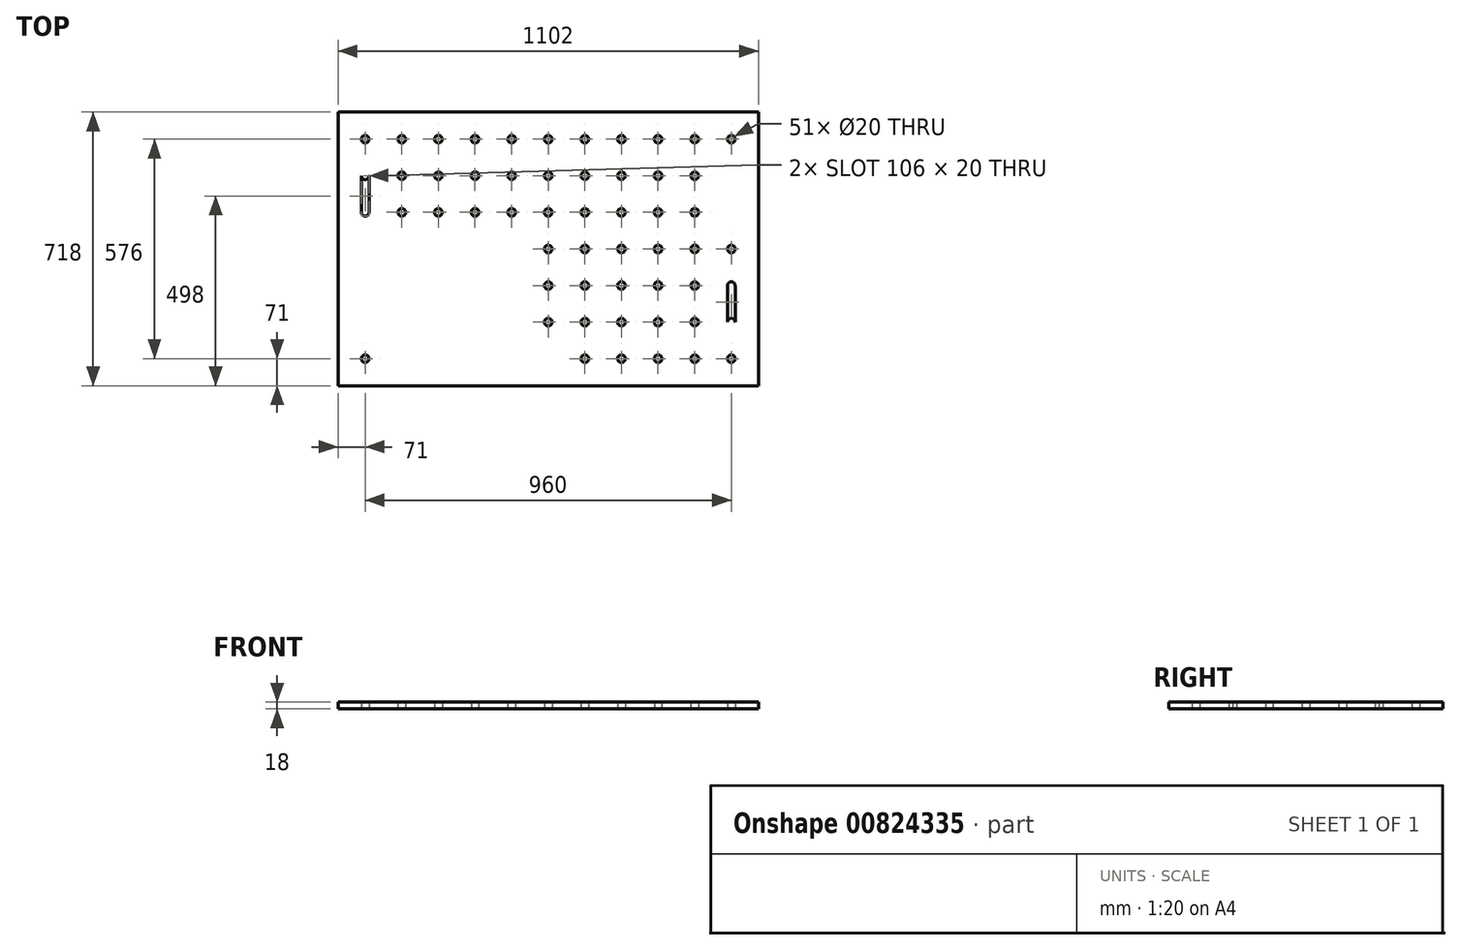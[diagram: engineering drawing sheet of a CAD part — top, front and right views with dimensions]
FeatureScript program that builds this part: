
annotation { "Feature Type Name" : "Feature", "Feature Type Description" : "" }
export const myFeature = defineFeature(function(context is Context, id is Id, definition is map)
    precondition{}
    {
        {
            var Q0;
            Q0=qCreatedBy(makeId("Top.planeOp"),FACE);
            var sketch = newSketch(context, id + "F0", { "sketchPlane" : qUnion([Q0])});
            skLineSegment(sketch, "E0.bottom", {"start": v(-551, -359) * mm, "end": v(551, -359) * mm});
            skLineSegment(sketch, "E0.top", {"start": v(-551, 359) * mm, "end": v(551, 359) * mm});
            skLineSegment(sketch, "E0.left", {"start": v(-551, -359) * mm, "end": v(-551, 359) * mm});
            skLineSegment(sketch, "E0.right", {"start": v(551, -359) * mm, "end": v(551, 359) * mm});
            skPoint(sketch, "E0.middle", {"position": v(0, 0) * mm});
            skSolve(sketch);
        }
        {
            var Q0;
            Q0=makeQuery(id+"F0.imprint","IMPRINT",FACE,{"disambiguationData":[TD([[makeQuery(id+"F0.imprint","IMPRINT",EDGE,{"derivedFrom":sQuery(id+"F0.wireOp",EDGE,"E0.bottom")}),1.0]])]});
            var sketch = newSketch(context, id + "F1", { "sketchPlane" : qUnion([Q0])});
            skLineSegment(sketch, "E1", {"start": v(0, 268.38) * mm, "end": v(0, -265.3) * mm, "construction": true});
            skLineSegment(sketch, "E2", {"start": v(473.2, 0) * mm, "end": v(-470.36, 0) * mm, "construction": true});
            skCircle(sketch, "E3", {"center": v(0, 0) * mm, "radius": 10 * mm});
            skCircle(sketch, "E4", {"center": v(96, 0) * mm, "radius": 10 * mm});
            skCircle(sketch, "E5.0.1.0", {"center": v(0, 96) * mm, "radius": 10 * mm});
            skCircle(sketch, "E5.0.1.1", {"center": v(96, 96) * mm, "radius": 10 * mm});
            skCircle(sketch, "E5.0.2.0", {"center": v(0, 192) * mm, "radius": 10 * mm});
            skCircle(sketch, "E5.0.2.1", {"center": v(96, 192) * mm, "radius": 10 * mm});
            skCircle(sketch, "E5.0.3.0", {"center": v(0, 288) * mm, "radius": 10 * mm});
            skCircle(sketch, "E5.0.3.1", {"center": v(96, 288) * mm, "radius": 10 * mm});
            skCircle(sketch, "E5.1.0.1", {"center": v(192, 0) * mm, "radius": 10 * mm});
            skCircle(sketch, "E5.1.1.0", {"center": v(96, 96) * mm, "radius": 10 * mm});
            skCircle(sketch, "E5.1.1.1", {"center": v(192, 96) * mm, "radius": 10 * mm});
            skCircle(sketch, "E5.1.2.0", {"center": v(96, 192) * mm, "radius": 10 * mm});
            skCircle(sketch, "E5.1.2.1", {"center": v(192, 192) * mm, "radius": 10 * mm});
            skCircle(sketch, "E5.1.3.0", {"center": v(96, 288) * mm, "radius": 10 * mm});
            skCircle(sketch, "E5.1.3.1", {"center": v(192, 288) * mm, "radius": 10 * mm});
            skCircle(sketch, "E5.2.0.0", {"center": v(192, 0) * mm, "radius": 10 * mm});
            skCircle(sketch, "E5.2.0.1", {"center": v(288, 0) * mm, "radius": 10 * mm});
            skCircle(sketch, "E5.2.1.0", {"center": v(192, 96) * mm, "radius": 10 * mm});
            skCircle(sketch, "E5.2.1.1", {"center": v(288, 96) * mm, "radius": 10 * mm});
            skCircle(sketch, "E5.2.2.0", {"center": v(192, 192) * mm, "radius": 10 * mm});
            skCircle(sketch, "E5.2.2.1", {"center": v(288, 192) * mm, "radius": 10 * mm});
            skCircle(sketch, "E5.2.3.0", {"center": v(192, 288) * mm, "radius": 10 * mm});
            skCircle(sketch, "E5.2.3.1", {"center": v(288, 288) * mm, "radius": 10 * mm});
            skCircle(sketch, "E5.3.0.0", {"center": v(288, 0) * mm, "radius": 10 * mm});
            skCircle(sketch, "E5.3.0.1", {"center": v(384, 0) * mm, "radius": 10 * mm});
            skCircle(sketch, "E5.3.1.0", {"center": v(288, 96) * mm, "radius": 10 * mm});
            skCircle(sketch, "E5.3.1.1", {"center": v(384, 96) * mm, "radius": 10 * mm});
            skCircle(sketch, "E5.3.2.0", {"center": v(288, 192) * mm, "radius": 10 * mm});
            skCircle(sketch, "E5.3.2.1", {"center": v(384, 192) * mm, "radius": 10 * mm});
            skCircle(sketch, "E5.3.3.0", {"center": v(288, 288) * mm, "radius": 10 * mm});
            skCircle(sketch, "E5.3.3.1", {"center": v(384, 288) * mm, "radius": 10 * mm});
            skCircle(sketch, "E5.4.0.0", {"center": v(384, 0) * mm, "radius": 10 * mm});
            skCircle(sketch, "E5.4.0.1", {"center": v(480, 0) * mm, "radius": 10 * mm});
            skCircle(sketch, "E5.4.1.0", {"center": v(384, 96) * mm, "radius": 10 * mm});
            skCircle(sketch, "E5.4.1.1", {"center": v(480, 96) * mm, "radius": 10 * mm});
            skCircle(sketch, "E5.4.2.0", {"center": v(384, 192) * mm, "radius": 10 * mm});
            skCircle(sketch, "E5.4.2.1", {"center": v(480, 192) * mm, "radius": 10 * mm});
            skCircle(sketch, "E5.4.3.0", {"center": v(384, 288) * mm, "radius": 10 * mm});
            skCircle(sketch, "E5.4.3.1", {"center": v(480, 288) * mm, "radius": 10 * mm});
            skLineSegment(sketch, "E5.direction1", {"start": v(0, 0) * mm, "end": v(96, 0) * mm, "construction": true});
            skLineSegment(sketch, "E5.direction2", {"start": v(0, 0) * mm, "end": v(0, 96) * mm, "construction": true});
            skCircle(sketch, "E6.MirrorC", {"center": v(-96, 0) * mm, "radius": 10 * mm});
            skCircle(sketch, "E7.MirrorC", {"center": v(-384, 0) * mm, "radius": 10 * mm});
            skCircle(sketch, "E8.MirrorC", {"center": v(-288, 192) * mm, "radius": 10 * mm});
            skCircle(sketch, "E9.MirrorC", {"center": v(-384, 96) * mm, "radius": 10 * mm});
            skCircle(sketch, "E10.MirrorC", {"center": v(-192, 96) * mm, "radius": 10 * mm});
            skCircle(sketch, "E11.MirrorC", {"center": v(-288, 288) * mm, "radius": 10 * mm});
            skCircle(sketch, "E12.MirrorC", {"center": v(-96, 288) * mm, "radius": 10 * mm});
            skCircle(sketch, "E13.MirrorC", {"center": v(-96, 192) * mm, "radius": 10 * mm});
            skCircle(sketch, "E14.MirrorC", {"center": v(-192, 192) * mm, "radius": 10 * mm});
            skCircle(sketch, "E15.MirrorC", {"center": v(-288, 96) * mm, "radius": 10 * mm});
            skCircle(sketch, "E16.MirrorC", {"center": v(-192, 288) * mm, "radius": 10 * mm});
            skCircle(sketch, "E17.MirrorC", {"center": v(-96, 96) * mm, "radius": 10 * mm});
            skCircle(sketch, "E18.MirrorC", {"center": v(-384, 288) * mm, "radius": 10 * mm});
            skCircle(sketch, "E19.MirrorC", {"center": v(-192, 0) * mm, "radius": 10 * mm});
            skCircle(sketch, "E20.MirrorC", {"center": v(-384, 192) * mm, "radius": 10 * mm});
            skCircle(sketch, "E21.MirrorC", {"center": v(-288, 0) * mm, "radius": 10 * mm});
            skCircle(sketch, "E22.MirrorC", {"center": v(-480, 192) * mm, "radius": 10 * mm});
            skCircle(sketch, "E23.MirrorC", {"center": v(-480, 96) * mm, "radius": 10 * mm});
            skCircle(sketch, "E24.MirrorC", {"center": v(-480, 288) * mm, "radius": 10 * mm});
            skCircle(sketch, "E25.MirrorC", {"center": v(-480, 0) * mm, "radius": 10 * mm});
            skLineSegment(sketch, "E26.MirrorCS", {"start": v(0, 0) * mm, "end": v(-96, 0) * mm, "construction": true});
            skCircle(sketch, "E27.MirrorC", {"center": v(0, -96) * mm, "radius": 10 * mm});
            skCircle(sketch, "E28.MirrorC", {"center": v(-96, -192) * mm, "radius": 10 * mm});
            skCircle(sketch, "E29.MirrorC", {"center": v(96, -192) * mm, "radius": 10 * mm});
            skCircle(sketch, "E30.MirrorC", {"center": v(-192, -96) * mm, "radius": 10 * mm});
            skCircle(sketch, "E31.MirrorC", {"center": v(-192, -288) * mm, "radius": 10 * mm});
            skCircle(sketch, "E32.MirrorC", {"center": v(0, -192) * mm, "radius": 10 * mm});
            skCircle(sketch, "E33.MirrorC", {"center": v(192, -192) * mm, "radius": 10 * mm});
            skCircle(sketch, "E34.MirrorC", {"center": v(384, -192) * mm, "radius": 10 * mm});
            skCircle(sketch, "E35.MirrorC", {"center": v(96, -288) * mm, "radius": 10 * mm});
            skCircle(sketch, "E36.MirrorC", {"center": v(288, -288) * mm, "radius": 10 * mm});
            skCircle(sketch, "E37.MirrorC", {"center": v(-288, -96) * mm, "radius": 10 * mm});
            skCircle(sketch, "E38.MirrorC", {"center": v(-288, -192) * mm, "radius": 10 * mm});
            skCircle(sketch, "E39.MirrorC", {"center": v(-384, -288) * mm, "radius": 10 * mm});
            skCircle(sketch, "E40.MirrorC", {"center": v(-384, -96) * mm, "radius": 10 * mm});
            skCircle(sketch, "E41.MirrorC", {"center": v(288, -192) * mm, "radius": 10 * mm});
            skCircle(sketch, "E42.MirrorC", {"center": v(-192, -192) * mm, "radius": 10 * mm});
            skCircle(sketch, "E43.MirrorC", {"center": v(-384, -192) * mm, "radius": 10 * mm});
            skCircle(sketch, "E44.MirrorC", {"center": v(288, -96) * mm, "radius": 10 * mm});
            skCircle(sketch, "E45.MirrorC", {"center": v(-96, -288) * mm, "radius": 10 * mm});
            skCircle(sketch, "E46.MirrorC", {"center": v(-96, -96) * mm, "radius": 10 * mm});
            skCircle(sketch, "E47.MirrorC", {"center": v(192, -96) * mm, "radius": 10 * mm});
            skCircle(sketch, "E48.MirrorC", {"center": v(384, -96) * mm, "radius": 10 * mm});
            skCircle(sketch, "E49.MirrorC", {"center": v(192, -288) * mm, "radius": 10 * mm});
            skCircle(sketch, "E50.MirrorC", {"center": v(96, -96) * mm, "radius": 10 * mm});
            skCircle(sketch, "E51.MirrorC", {"center": v(-288, -288) * mm, "radius": 10 * mm});
            skCircle(sketch, "E52.MirrorC", {"center": v(384, -288) * mm, "radius": 10 * mm});
            skCircle(sketch, "E53.MirrorC", {"center": v(0, -288) * mm, "radius": 10 * mm});
            skCircle(sketch, "E54.MirrorC", {"center": v(-480, -192) * mm, "radius": 10 * mm});
            skCircle(sketch, "E55.MirrorC", {"center": v(480, -96) * mm, "radius": 10 * mm});
            skCircle(sketch, "E56.MirrorC", {"center": v(480, -192) * mm, "radius": 10 * mm});
            skLineSegment(sketch, "E57.MirrorCS", {"start": v(0, 0) * mm, "end": v(0, -96) * mm, "construction": true});
            skCircle(sketch, "E58.MirrorC", {"center": v(-480, -96) * mm, "radius": 10 * mm});
            skCircle(sketch, "E59.MirrorC", {"center": v(480, -288) * mm, "radius": 10 * mm});
            skCircle(sketch, "E60.MirrorC", {"center": v(-480, -288) * mm, "radius": 10 * mm});
            skLineSegment(sketch, "E61", {"start": v(480, 288) * mm, "end": v(480, 96) * mm});
            skArc(sketch, "E62.0.startCap", {"start": v(470, 288) * mm, "mid": v(480, 298) * mm, "end": v(490, 288) * mm});
            skArc(sketch, "E62.0.endCap", {"start": v(490, 96) * mm, "mid": v(480, 86) * mm, "end": v(470, 96) * mm});
            skLineSegment(sketch, "E62.0.left", {"start": v(490, 288) * mm, "end": v(490, 96) * mm});
            skLineSegment(sketch, "E62.0.right", {"start": v(470, 288) * mm, "end": v(470, 96) * mm});
            skLineSegment(sketch, "E63", {"start": v(480, -96) * mm, "end": v(480, -288) * mm});
            skLineSegment(sketch, "E64", {"start": v(-480, -96) * mm, "end": v(-480, -288) * mm});
            skLineSegment(sketch, "E65", {"start": v(-480, 288) * mm, "end": v(-480, 96) * mm});
            skArc(sketch, "E66.0.startCap", {"start": v(-490, 288) * mm, "mid": v(-480, 298) * mm, "end": v(-470, 288) * mm});
            skArc(sketch, "E66.0.endCap", {"start": v(-470, 96) * mm, "mid": v(-480, 86) * mm, "end": v(-490, 96) * mm});
            skLineSegment(sketch, "E66.0.left", {"start": v(-470, 288) * mm, "end": v(-470, 96) * mm});
            skLineSegment(sketch, "E66.0.right", {"start": v(-490, 288) * mm, "end": v(-490, 96) * mm});
            skArc(sketch, "E66.1.startCap", {"start": v(-490, -96) * mm, "mid": v(-480, -86) * mm, "end": v(-470, -96) * mm});
            skArc(sketch, "E66.1.endCap", {"start": v(-470, -288) * mm, "mid": v(-480, -298) * mm, "end": v(-490, -288) * mm});
            skLineSegment(sketch, "E66.1.left", {"start": v(-470, -96) * mm, "end": v(-470, -288) * mm});
            skLineSegment(sketch, "E66.1.right", {"start": v(-490, -96) * mm, "end": v(-490, -288) * mm});
            skArc(sketch, "E67.0.startCap", {"start": v(470, -96) * mm, "mid": v(480, -86) * mm, "end": v(490, -96) * mm});
            skArc(sketch, "E67.0.endCap", {"start": v(490, -288) * mm, "mid": v(480, -298) * mm, "end": v(470, -288) * mm});
            skLineSegment(sketch, "E67.0.left", {"start": v(490, -96) * mm, "end": v(490, -288) * mm});
            skLineSegment(sketch, "E67.0.right", {"start": v(470, -96) * mm, "end": v(470, -288) * mm});
            skSolve(sketch);
        }
        {
            var Q0;
            {var subQ0=sQuery(id+"F1.wireOp",EDGE,"E65");var subQ1=sQuery(id+"F1.wireOp",EDGE,"E22.MirrorC");var subQ2=makeQuery(id+"F1.imprint","INTERSECT",VERTEX,{"disambiguationData":[OD(0.0)],"derivedFrom":[subQ1,subQ0]});Q0=makeQuery(id+"F1.imprint","IMPRINT",FACE,{"disambiguationData":[TD([[makeQuery(id+"F1.imprint","IMPRINT",EDGE,{"disambiguationData":[TD([[subQ2,1.0]])],"derivedFrom":subQ1}),1.0]])]});}
            var Q1;
            {var subQ0=sQuery(id+"F1.wireOp",EDGE,"E63");var subQ1=sQuery(id+"F1.wireOp",EDGE,"E56.MirrorC");var subQ2=makeQuery(id+"F1.imprint","INTERSECT",VERTEX,{"disambiguationData":[OD(0.0)],"derivedFrom":[subQ1,subQ0]});Q1=makeQuery(id+"F1.imprint","IMPRINT",FACE,{"disambiguationData":[TD([[makeQuery(id+"F1.imprint","IMPRINT",EDGE,{"disambiguationData":[TD([[subQ2,-1.0]])],"derivedFrom":subQ1}),1.0]])]});}
            var Q2;
            Q2=makeQuery(id+"F1.imprint","IMPRINT",FACE,{"disambiguationData":[TD([[makeQuery(id+"F1.imprint","IMPRINT",EDGE,{"derivedFrom":sQuery(id+"F1.wireOp",EDGE,"E5.1.1.0")}),-1.0]])]});
            var Q3;
            {var subQ0=sQuery(id+"F1.wireOp",EDGE,"E62.0.right");var subQ1=sQuery(id+"F1.wireOp",EDGE,"E5.4.1.1");var subQ2=makeQuery(id+"F1.imprint","INTERSECT",VERTEX,{"derivedFrom":[subQ1,subQ0]});Q3=makeQuery(id+"F1.imprint","IMPRINT",FACE,{"disambiguationData":[TD([[makeQuery(id+"F1.imprint","IMPRINT",EDGE,{"disambiguationData":[TD([[subQ2,1.0]])],"derivedFrom":subQ1}),-1.0]])]});}
            var Q4;
            Q4=makeQuery(id+"F0.imprint","IMPRINT",FACE,{"disambiguationData":[TD([[makeQuery(id+"F0.imprint","IMPRINT",EDGE,{"derivedFrom":sQuery(id+"F0.wireOp",EDGE,"E0.bottom")}),1.0]])]});
            var Q5;
            {var subQ0=sQuery(id+"F1.wireOp",EDGE,"E66.0.right");var subQ1=sQuery(id+"F1.wireOp",EDGE,"E22.MirrorC");var subQ2=makeQuery(id+"F1.imprint","INTERSECT",VERTEX,{"derivedFrom":[subQ1,subQ0]});Q5=makeQuery(id+"F1.imprint","IMPRINT",FACE,{"disambiguationData":[TD([[makeQuery(id+"F1.imprint","IMPRINT",EDGE,{"disambiguationData":[TD([[subQ2,1.0]])],"derivedFrom":subQ1}),1.0]])]});}
            var Q6;
            {var subQ0=sQuery(id+"F1.wireOp",EDGE,"E64");var subQ1=sQuery(id+"F1.wireOp",EDGE,"E54.MirrorC");var subQ2=makeQuery(id+"F1.imprint","INTERSECT",VERTEX,{"disambiguationData":[OD(0.0)],"derivedFrom":[subQ1,subQ0]});Q6=makeQuery(id+"F1.imprint","IMPRINT",FACE,{"disambiguationData":[TD([[makeQuery(id+"F1.imprint","IMPRINT",EDGE,{"disambiguationData":[TD([[subQ2,1.0]])],"derivedFrom":subQ1}),-1.0]])]});}
            var Q7;
            {var subQ0=sQuery(id+"F1.wireOp",EDGE,"E61");var subQ1=sQuery(id+"F1.wireOp",EDGE,"E5.4.2.1");var subQ2=makeQuery(id+"F1.imprint","INTERSECT",VERTEX,{"disambiguationData":[OD(0.0)],"derivedFrom":[subQ1,subQ0]});Q7=makeQuery(id+"F1.imprint","IMPRINT",FACE,{"disambiguationData":[TD([[makeQuery(id+"F1.imprint","IMPRINT",EDGE,{"disambiguationData":[TD([[subQ2,-1.0]])],"derivedFrom":subQ1}),-1.0]])]});}
            var Q8;
            {var subQ0=sQuery(id+"F1.wireOp",EDGE,"E66.1.right");var subQ1=sQuery(id+"F1.wireOp",EDGE,"E54.MirrorC");var subQ2=makeQuery(id+"F1.imprint","INTERSECT",VERTEX,{"derivedFrom":[subQ1,subQ0]});Q8=makeQuery(id+"F1.imprint","IMPRINT",FACE,{"disambiguationData":[TD([[makeQuery(id+"F1.imprint","IMPRINT",EDGE,{"disambiguationData":[TD([[subQ2,1.0]])],"derivedFrom":subQ1}),-1.0]])]});}
            var Q9;
            {var subQ0=sQuery(id+"F1.wireOp",EDGE,"E67.0.right");var subQ1=sQuery(id+"F1.wireOp",EDGE,"E55.MirrorC");var subQ2=makeQuery(id+"F1.imprint","INTERSECT",VERTEX,{"derivedFrom":[subQ1,subQ0]});Q9=makeQuery(id+"F1.imprint","IMPRINT",FACE,{"disambiguationData":[TD([[makeQuery(id+"F1.imprint","IMPRINT",EDGE,{"disambiguationData":[TD([[subQ2,1.0]])],"derivedFrom":subQ1}),1.0]])]});}
            var Q10;
            {var subQ0=sQuery(id+"F1.wireOp",EDGE,"E62.0.left");var subQ1=sQuery(id+"F1.wireOp",EDGE,"E5.4.1.1");var subQ2=makeQuery(id+"F1.imprint","INTERSECT",VERTEX,{"derivedFrom":[subQ1,subQ0]});Q10=makeQuery(id+"F1.imprint","IMPRINT",FACE,{"disambiguationData":[TD([[makeQuery(id+"F1.imprint","IMPRINT",EDGE,{"disambiguationData":[TD([[subQ2,-1.0]])],"derivedFrom":subQ1}),-1.0]])]});}
            var Q11;
            {var subQ0=sQuery(id+"F1.wireOp",EDGE,"E65");var subQ1=sQuery(id+"F1.wireOp",EDGE,"E22.MirrorC");var subQ2=makeQuery(id+"F1.imprint","INTERSECT",VERTEX,{"disambiguationData":[OD(0.0)],"derivedFrom":[subQ1,subQ0]});Q11=makeQuery(id+"F1.imprint","IMPRINT",FACE,{"disambiguationData":[TD([[makeQuery(id+"F1.imprint","IMPRINT",EDGE,{"disambiguationData":[TD([[subQ2,-1.0]])],"derivedFrom":subQ1}),1.0]])]});}
            var Q12;
            {var subQ0=sQuery(id+"F1.wireOp",EDGE,"E66.0.left");var subQ1=sQuery(id+"F1.wireOp",EDGE,"E22.MirrorC");var subQ2=makeQuery(id+"F1.imprint","INTERSECT",VERTEX,{"derivedFrom":[subQ1,subQ0]});Q12=makeQuery(id+"F1.imprint","IMPRINT",FACE,{"disambiguationData":[TD([[makeQuery(id+"F1.imprint","IMPRINT",EDGE,{"disambiguationData":[TD([[subQ2,-1.0]])],"derivedFrom":subQ1}),1.0]])]});}
            var Q13;
            {var subQ0=sQuery(id+"F1.wireOp",EDGE,"E61");var subQ1=sQuery(id+"F1.wireOp",EDGE,"E5.4.2.1");var subQ2=makeQuery(id+"F1.imprint","INTERSECT",VERTEX,{"disambiguationData":[OD(0.0)],"derivedFrom":[subQ1,subQ0]});Q13=makeQuery(id+"F1.imprint","IMPRINT",FACE,{"disambiguationData":[TD([[makeQuery(id+"F1.imprint","IMPRINT",EDGE,{"disambiguationData":[TD([[subQ2,1.0]])],"derivedFrom":subQ1}),-1.0]])]});}
            var Q14;
            {var subQ0=sQuery(id+"F1.wireOp",EDGE,"E64");var subQ1=sQuery(id+"F1.wireOp",EDGE,"E54.MirrorC");var subQ2=makeQuery(id+"F1.imprint","INTERSECT",VERTEX,{"disambiguationData":[OD(0.0)],"derivedFrom":[subQ1,subQ0]});Q14=makeQuery(id+"F1.imprint","IMPRINT",FACE,{"disambiguationData":[TD([[makeQuery(id+"F1.imprint","IMPRINT",EDGE,{"disambiguationData":[TD([[subQ2,1.0]])],"derivedFrom":subQ1}),1.0]])]});}
            var Q15;
            {var subQ0=sQuery(id+"F1.wireOp",EDGE,"E63");var subQ1=sQuery(id+"F1.wireOp",EDGE,"E56.MirrorC");var subQ2=makeQuery(id+"F1.imprint","INTERSECT",VERTEX,{"disambiguationData":[OD(0.0)],"derivedFrom":[subQ1,subQ0]});Q15=makeQuery(id+"F1.imprint","IMPRINT",FACE,{"disambiguationData":[TD([[makeQuery(id+"F1.imprint","IMPRINT",EDGE,{"disambiguationData":[TD([[subQ2,1.0]])],"derivedFrom":subQ1}),1.0]])]});}
            var Q16;
            {var subQ0=sQuery(id+"F1.wireOp",EDGE,"E66.1.left");var subQ1=sQuery(id+"F1.wireOp",EDGE,"E54.MirrorC");var subQ2=makeQuery(id+"F1.imprint","INTERSECT",VERTEX,{"derivedFrom":[subQ1,subQ0]});Q16=makeQuery(id+"F1.imprint","IMPRINT",FACE,{"disambiguationData":[TD([[makeQuery(id+"F1.imprint","IMPRINT",EDGE,{"disambiguationData":[TD([[subQ2,-1.0]])],"derivedFrom":subQ1}),-1.0]])]});}
            var Q17;
            {var subQ0=sQuery(id+"F1.wireOp",EDGE,"E67.0.left");var subQ1=sQuery(id+"F1.wireOp",EDGE,"E55.MirrorC");var subQ2=makeQuery(id+"F1.imprint","INTERSECT",VERTEX,{"derivedFrom":[subQ1,subQ0]});Q17=makeQuery(id+"F1.imprint","IMPRINT",FACE,{"disambiguationData":[TD([[makeQuery(id+"F1.imprint","IMPRINT",EDGE,{"disambiguationData":[TD([[subQ2,-1.0]])],"derivedFrom":subQ1}),1.0]])]});}
            var Q18;
            {var subQ0=sQuery(id+"F1.wireOp",EDGE,"E64");var subQ1=sQuery(id+"F1.wireOp",EDGE,"E54.MirrorC");var subQ2=makeQuery(id+"F1.imprint","INTERSECT",VERTEX,{"disambiguationData":[OD(0.0)],"derivedFrom":[subQ1,subQ0]});Q18=makeQuery(id+"F1.imprint","IMPRINT",FACE,{"disambiguationData":[TD([[makeQuery(id+"F1.imprint","IMPRINT",EDGE,{"disambiguationData":[TD([[subQ2,-1.0]])],"derivedFrom":subQ1}),-1.0]])]});}
            var Q19;
            Q19=makeQuery(id+"F1.imprint","IMPRINT",FACE,{"disambiguationData":[TD([[makeQuery(id+"F1.imprint","IMPRINT",EDGE,{"derivedFrom":sQuery(id+"F1.wireOp",EDGE,"E32.MirrorC")}),-1.0]])]});
            var Q20;
            Q20=makeQuery(id+"F1.imprint","IMPRINT",FACE,{"disambiguationData":[TD([[makeQuery(id+"F1.imprint","IMPRINT",EDGE,{"derivedFrom":sQuery(id+"F1.wireOp",EDGE,"E43.MirrorC")}),1.0]])]});
            var Q21;
            {var subQ0=sQuery(id+"F1.wireOp",EDGE,"E65");var subQ1=sQuery(id+"F1.wireOp",EDGE,"E22.MirrorC");var subQ2=makeQuery(id+"F1.imprint","INTERSECT",VERTEX,{"disambiguationData":[OD(0.0)],"derivedFrom":[subQ1,subQ0]});Q21=makeQuery(id+"F1.imprint","IMPRINT",FACE,{"disambiguationData":[TD([[makeQuery(id+"F1.imprint","IMPRINT",EDGE,{"disambiguationData":[TD([[subQ2,1.0]])],"derivedFrom":subQ1}),-1.0]])]});}
            var Q22;
            Q22=makeQuery(id+"F1.imprint","IMPRINT",FACE,{"disambiguationData":[TD([[makeQuery(id+"F1.imprint","IMPRINT",EDGE,{"derivedFrom":sQuery(id+"F1.wireOp",EDGE,"E52.MirrorC")}),-1.0]])]});
            var Q23;
            Q23=makeQuery(id+"F1.imprint","IMPRINT",FACE,{"disambiguationData":[TD([[makeQuery(id+"F1.imprint","IMPRINT",EDGE,{"derivedFrom":sQuery(id+"F1.wireOp",EDGE,"E47.MirrorC")}),-1.0]])]});
            var Q24;
            Q24=makeQuery(id+"F1.imprint","IMPRINT",FACE,{"disambiguationData":[TD([[makeQuery(id+"F1.imprint","IMPRINT",EDGE,{"derivedFrom":sQuery(id+"F1.wireOp",EDGE,"E25.MirrorC")}),1.0]])]});
            var Q25;
            Q25=makeQuery(id+"F1.imprint","IMPRINT",FACE,{"disambiguationData":[TD([[makeQuery(id+"F1.imprint","IMPRINT",EDGE,{"derivedFrom":sQuery(id+"F1.wireOp",EDGE,"E49.MirrorC")}),-1.0]])]});
            var Q26;
            Q26=makeQuery(id+"F1.imprint","IMPRINT",FACE,{"disambiguationData":[TD([[makeQuery(id+"F1.imprint","IMPRINT",EDGE,{"derivedFrom":sQuery(id+"F1.wireOp",EDGE,"E34.MirrorC")}),-1.0]])]});
            var Q27;
            {var subQ0=sQuery(id+"F1.wireOp",EDGE,"E65");var subQ1=sQuery(id+"F1.wireOp",EDGE,"E22.MirrorC");var subQ2=makeQuery(id+"F1.imprint","INTERSECT",VERTEX,{"disambiguationData":[OD(0.0)],"derivedFrom":[subQ1,subQ0]});Q27=makeQuery(id+"F1.imprint","IMPRINT",FACE,{"disambiguationData":[TD([[makeQuery(id+"F1.imprint","IMPRINT",EDGE,{"disambiguationData":[TD([[subQ2,-1.0]])],"derivedFrom":subQ1}),-1.0]])]});}
            var Q28;
            Q28=makeQuery(id+"F1.imprint","IMPRINT",FACE,{"disambiguationData":[TD([[makeQuery(id+"F1.imprint","IMPRINT",EDGE,{"derivedFrom":sQuery(id+"F1.wireOp",EDGE,"E39.MirrorC")}),1.0]])]});
            var Q29;
            Q29=makeQuery(id+"F1.imprint","IMPRINT",FACE,{"disambiguationData":[TD([[makeQuery(id+"F1.imprint","IMPRINT",EDGE,{"derivedFrom":sQuery(id+"F1.wireOp",EDGE,"E50.MirrorC")}),-1.0]])]});
            var Q30;
            Q30=makeQuery(id+"F1.imprint","IMPRINT",FACE,{"disambiguationData":[TD([[makeQuery(id+"F1.imprint","IMPRINT",EDGE,{"derivedFrom":sQuery(id+"F1.wireOp",EDGE,"E40.MirrorC")}),1.0]])]});
            var Q31;
            {var subQ0=sQuery(id+"F1.wireOp",EDGE,"E61");var subQ1=sQuery(id+"F1.wireOp",EDGE,"E5.4.2.1");var subQ2=makeQuery(id+"F1.imprint","INTERSECT",VERTEX,{"disambiguationData":[OD(0.0)],"derivedFrom":[subQ1,subQ0]});Q31=makeQuery(id+"F1.imprint","IMPRINT",FACE,{"disambiguationData":[TD([[makeQuery(id+"F1.imprint","IMPRINT",EDGE,{"disambiguationData":[TD([[subQ2,1.0]])],"derivedFrom":subQ1}),1.0]])]});}
            var Q32;
            Q32=makeQuery(id+"F1.imprint","IMPRINT",FACE,{"disambiguationData":[TD([[makeQuery(id+"F1.imprint","IMPRINT",EDGE,{"derivedFrom":sQuery(id+"F1.wireOp",EDGE,"E51.MirrorC")}),1.0]])]});
            var Q33;
            Q33=makeQuery(id+"F1.imprint","IMPRINT",FACE,{"disambiguationData":[TD([[makeQuery(id+"F1.imprint","IMPRINT",EDGE,{"derivedFrom":sQuery(id+"F1.wireOp",EDGE,"E31.MirrorC")}),1.0]])]});
            var Q34;
            Q34=makeQuery(id+"F1.imprint","IMPRINT",FACE,{"disambiguationData":[TD([[makeQuery(id+"F1.imprint","IMPRINT",EDGE,{"derivedFrom":sQuery(id+"F1.wireOp",EDGE,"E53.MirrorC")}),1.0]])]});
            var Q35;
            Q35=makeQuery(id+"F1.imprint","IMPRINT",FACE,{"disambiguationData":[TD([[makeQuery(id+"F1.imprint","IMPRINT",EDGE,{"derivedFrom":sQuery(id+"F1.wireOp",EDGE,"E44.MirrorC")}),-1.0]])]});
            var Q36;
            Q36=makeQuery(id+"F1.imprint","IMPRINT",FACE,{"disambiguationData":[TD([[makeQuery(id+"F1.imprint","IMPRINT",EDGE,{"derivedFrom":sQuery(id+"F1.wireOp",EDGE,"E41.MirrorC")}),-1.0]])]});
            var Q37;
            {var subQ0=sQuery(id+"F1.wireOp",EDGE,"E61");var subQ1=sQuery(id+"F1.wireOp",EDGE,"E5.4.2.1");var subQ2=makeQuery(id+"F1.imprint","INTERSECT",VERTEX,{"disambiguationData":[OD(0.0)],"derivedFrom":[subQ1,subQ0]});Q37=makeQuery(id+"F1.imprint","IMPRINT",FACE,{"disambiguationData":[TD([[makeQuery(id+"F1.imprint","IMPRINT",EDGE,{"disambiguationData":[TD([[subQ2,-1.0]])],"derivedFrom":subQ1}),1.0]])]});}
            var Q38;
            Q38=makeQuery(id+"F1.imprint","IMPRINT",FACE,{"disambiguationData":[TD([[makeQuery(id+"F1.imprint","IMPRINT",EDGE,{"derivedFrom":sQuery(id+"F1.wireOp",EDGE,"E30.MirrorC")}),1.0]])]});
            var Q39;
            Q39=makeQuery(id+"F1.imprint","IMPRINT",FACE,{"disambiguationData":[TD([[makeQuery(id+"F1.imprint","IMPRINT",EDGE,{"derivedFrom":sQuery(id+"F1.wireOp",EDGE,"E36.MirrorC")}),-1.0]])]});
            var Q40;
            Q40=makeQuery(id+"F1.imprint","IMPRINT",FACE,{"disambiguationData":[TD([[makeQuery(id+"F1.imprint","IMPRINT",EDGE,{"derivedFrom":sQuery(id+"F1.wireOp",EDGE,"E48.MirrorC")}),-1.0]])]});
            var Q41;
            Q41=makeQuery(id+"F1.imprint","IMPRINT",FACE,{"disambiguationData":[TD([[makeQuery(id+"F1.imprint","IMPRINT",EDGE,{"derivedFrom":sQuery(id+"F1.wireOp",EDGE,"E45.MirrorC")}),1.0]])]});
            var Q42;
            {var subQ0=sQuery(id+"F1.wireOp",EDGE,"E63");var subQ1=sQuery(id+"F1.wireOp",EDGE,"E56.MirrorC");var subQ2=makeQuery(id+"F1.imprint","INTERSECT",VERTEX,{"disambiguationData":[OD(0.0)],"derivedFrom":[subQ1,subQ0]});Q42=makeQuery(id+"F1.imprint","IMPRINT",FACE,{"disambiguationData":[TD([[makeQuery(id+"F1.imprint","IMPRINT",EDGE,{"disambiguationData":[TD([[subQ2,1.0]])],"derivedFrom":subQ1}),-1.0]])]});}
            var Q43;
            Q43=makeQuery(id+"F1.imprint","IMPRINT",FACE,{"disambiguationData":[TD([[makeQuery(id+"F1.imprint","IMPRINT",EDGE,{"derivedFrom":sQuery(id+"F1.wireOp",EDGE,"E37.MirrorC")}),1.0]])]});
            var Q44;
            Q44=makeQuery(id+"F1.imprint","IMPRINT",FACE,{"disambiguationData":[TD([[makeQuery(id+"F1.imprint","IMPRINT",EDGE,{"derivedFrom":sQuery(id+"F1.wireOp",EDGE,"E28.MirrorC")}),1.0]])]});
            var Q45;
            Q45=makeQuery(id+"F1.imprint","IMPRINT",FACE,{"disambiguationData":[TD([[makeQuery(id+"F1.imprint","IMPRINT",EDGE,{"derivedFrom":sQuery(id+"F1.wireOp",EDGE,"E35.MirrorC")}),-1.0]])]});
            var Q46;
            Q46=makeQuery(id+"F1.imprint","IMPRINT",FACE,{"disambiguationData":[TD([[makeQuery(id+"F1.imprint","IMPRINT",EDGE,{"derivedFrom":sQuery(id+"F1.wireOp",EDGE,"E46.MirrorC")}),1.0]])]});
            var Q47;
            Q47=makeQuery(id+"F1.imprint","IMPRINT",FACE,{"disambiguationData":[TD([[makeQuery(id+"F1.imprint","IMPRINT",EDGE,{"derivedFrom":sQuery(id+"F1.wireOp",EDGE,"E42.MirrorC")}),1.0]])]});
            var Q48;
            {var subQ0=sQuery(id+"F1.wireOp",EDGE,"E63");var subQ1=sQuery(id+"F1.wireOp",EDGE,"E56.MirrorC");var subQ2=makeQuery(id+"F1.imprint","INTERSECT",VERTEX,{"disambiguationData":[OD(0.0)],"derivedFrom":[subQ1,subQ0]});Q48=makeQuery(id+"F1.imprint","IMPRINT",FACE,{"disambiguationData":[TD([[makeQuery(id+"F1.imprint","IMPRINT",EDGE,{"disambiguationData":[TD([[subQ2,-1.0]])],"derivedFrom":subQ1}),-1.0]])]});}
            var Q49;
            Q49=makeQuery(id+"F1.imprint","IMPRINT",FACE,{"disambiguationData":[TD([[makeQuery(id+"F1.imprint","IMPRINT",EDGE,{"derivedFrom":sQuery(id+"F1.wireOp",EDGE,"E29.MirrorC")}),-1.0]])]});
            var Q50;
            {var subQ0=sQuery(id+"F1.wireOp",EDGE,"E64");var subQ1=sQuery(id+"F1.wireOp",EDGE,"E54.MirrorC");var subQ2=makeQuery(id+"F1.imprint","INTERSECT",VERTEX,{"disambiguationData":[OD(0.0)],"derivedFrom":[subQ1,subQ0]});Q50=makeQuery(id+"F1.imprint","IMPRINT",FACE,{"disambiguationData":[TD([[makeQuery(id+"F1.imprint","IMPRINT",EDGE,{"disambiguationData":[TD([[subQ2,-1.0]])],"derivedFrom":subQ1}),1.0]])]});}
            var Q51;
            Q51=makeQuery(id+"F1.imprint","IMPRINT",FACE,{"disambiguationData":[TD([[makeQuery(id+"F1.imprint","IMPRINT",EDGE,{"derivedFrom":sQuery(id+"F1.wireOp",EDGE,"E38.MirrorC")}),1.0]])]});
            var Q52;
            Q52=makeQuery(id+"F1.imprint","IMPRINT",FACE,{"disambiguationData":[TD([[makeQuery(id+"F1.imprint","IMPRINT",EDGE,{"derivedFrom":sQuery(id+"F1.wireOp",EDGE,"E33.MirrorC")}),-1.0]])]});
            var Q53;
            {var subQ0=sQuery(id+"F1.wireOp",EDGE,"E60.MirrorC");var subQ1=makeQuery(id+"F1.imprint","INTERSECT",VERTEX,{"derivedFrom":[subQ0,sQuery(id+"F1.wireOp",EDGE,"E66.1.left")]});Q53=makeQuery(id+"F1.imprint","IMPRINT",FACE,{"disambiguationData":[TD([[makeQuery(id+"F1.imprint","IMPRINT",EDGE,{"disambiguationData":[TD([[subQ1,1.0]])],"derivedFrom":subQ0}),1.0]])]});}
            var Q54;
            {var subQ0=sQuery(id+"F1.wireOp",EDGE,"E59.MirrorC");var subQ1=makeQuery(id+"F1.imprint","INTERSECT",VERTEX,{"derivedFrom":[subQ0,sQuery(id+"F1.wireOp",EDGE,"E67.0.left")]});Q54=makeQuery(id+"F1.imprint","IMPRINT",FACE,{"disambiguationData":[TD([[makeQuery(id+"F1.imprint","IMPRINT",EDGE,{"disambiguationData":[TD([[subQ1,-1.0]])],"derivedFrom":subQ0}),-1.0]])]});}
            var Q55;
            {var subQ0=sQuery(id+"F1.wireOp",EDGE,"E58.MirrorC");var subQ1=makeQuery(id+"F1.imprint","INTERSECT",VERTEX,{"derivedFrom":[subQ0,sQuery(id+"F1.wireOp",EDGE,"E66.1.right")]});Q55=makeQuery(id+"F1.imprint","IMPRINT",FACE,{"disambiguationData":[TD([[makeQuery(id+"F1.imprint","IMPRINT",EDGE,{"disambiguationData":[TD([[subQ1,-1.0]])],"derivedFrom":subQ0}),1.0]])]});}
            var Q56;
            Q56=makeQuery(id+"F1.imprint","IMPRINT",FACE,{"disambiguationData":[TD([[makeQuery(id+"F1.imprint","IMPRINT",EDGE,{"derivedFrom":sQuery(id+"F1.wireOp",EDGE,"E19.MirrorC")}),1.0]])]});
            var Q57;
            Q57=makeQuery(id+"F1.imprint","IMPRINT",FACE,{"disambiguationData":[TD([[makeQuery(id+"F1.imprint","IMPRINT",EDGE,{"derivedFrom":sQuery(id+"F1.wireOp",EDGE,"E17.MirrorC")}),-1.0]])]});
            var Q58;
            Q58=makeQuery(id+"F1.imprint","IMPRINT",FACE,{"disambiguationData":[TD([[makeQuery(id+"F1.imprint","IMPRINT",EDGE,{"derivedFrom":sQuery(id+"F1.wireOp",EDGE,"E8.MirrorC")}),-1.0]])]});
            var Q59;
            Q59=makeQuery(id+"F1.imprint","IMPRINT",FACE,{"disambiguationData":[TD([[makeQuery(id+"F1.imprint","IMPRINT",EDGE,{"derivedFrom":sQuery(id+"F1.wireOp",EDGE,"E15.MirrorC")}),-1.0]])]});
            var Q60;
            {var subQ0=sQuery(id+"F1.wireOp",EDGE,"E5.4.1.1");var subQ1=makeQuery(id+"F1.imprint","INTERSECT",VERTEX,{"derivedFrom":[subQ0,sQuery(id+"F1.wireOp",EDGE,"E62.0.left")]});Q60=makeQuery(id+"F1.imprint","IMPRINT",FACE,{"disambiguationData":[TD([[makeQuery(id+"F1.imprint","IMPRINT",EDGE,{"disambiguationData":[TD([[subQ1,-1.0]])],"derivedFrom":subQ0}),1.0]])]});}
            var Q61;
            Q61=makeQuery(id+"F1.imprint","IMPRINT",FACE,{"disambiguationData":[TD([[makeQuery(id+"F1.imprint","IMPRINT",EDGE,{"derivedFrom":sQuery(id+"F1.wireOp",EDGE,"E21.MirrorC")}),1.0]])]});
            var Q62;
            Q62=makeQuery(id+"F1.imprint","IMPRINT",FACE,{"disambiguationData":[TD([[makeQuery(id+"F1.imprint","IMPRINT",EDGE,{"derivedFrom":sQuery(id+"F1.wireOp",EDGE,"E11.MirrorC")}),-1.0]])]});
            var Q63;
            Q63=makeQuery(id+"F1.imprint","IMPRINT",FACE,{"disambiguationData":[TD([[makeQuery(id+"F1.imprint","IMPRINT",EDGE,{"derivedFrom":sQuery(id+"F1.wireOp",EDGE,"E12.MirrorC")}),-1.0]])]});
            var Q64;
            Q64=makeQuery(id+"F1.imprint","IMPRINT",FACE,{"disambiguationData":[TD([[makeQuery(id+"F1.imprint","IMPRINT",EDGE,{"derivedFrom":sQuery(id+"F1.wireOp",EDGE,"E20.MirrorC")}),-1.0]])]});
            var Q65;
            {var subQ0=sQuery(id+"F1.wireOp",EDGE,"E23.MirrorC");var subQ1=makeQuery(id+"F1.imprint","INTERSECT",VERTEX,{"derivedFrom":[subQ0,sQuery(id+"F1.wireOp",EDGE,"E66.0.right")]});Q65=makeQuery(id+"F1.imprint","IMPRINT",FACE,{"disambiguationData":[TD([[makeQuery(id+"F1.imprint","IMPRINT",EDGE,{"disambiguationData":[TD([[subQ1,-1.0]])],"derivedFrom":subQ0}),-1.0]])]});}
            var Q66;
            Q66=makeQuery(id+"F1.imprint","IMPRINT",FACE,{"disambiguationData":[TD([[makeQuery(id+"F1.imprint","IMPRINT",EDGE,{"derivedFrom":sQuery(id+"F1.wireOp",EDGE,"E13.MirrorC")}),-1.0]])]});
            var Q67;
            Q67=makeQuery(id+"F1.imprint","IMPRINT",FACE,{"disambiguationData":[TD([[makeQuery(id+"F1.imprint","IMPRINT",EDGE,{"derivedFrom":sQuery(id+"F1.wireOp",EDGE,"E10.MirrorC")}),-1.0]])]});
            var Q68;
            Q68=makeQuery(id+"F1.imprint","IMPRINT",FACE,{"disambiguationData":[TD([[makeQuery(id+"F1.imprint","IMPRINT",EDGE,{"derivedFrom":sQuery(id+"F1.wireOp",EDGE,"E5.1.1.0")}),1.0]])]});
            var Q69;
            Q69=makeQuery(id+"F1.imprint","IMPRINT",FACE,{"disambiguationData":[TD([[makeQuery(id+"F1.imprint","IMPRINT",EDGE,{"derivedFrom":sQuery(id+"F1.wireOp",EDGE,"E5.1.3.0")}),1.0]])]});
            var Q70;
            Q70=makeQuery(id+"F1.imprint","IMPRINT",FACE,{"disambiguationData":[TD([[makeQuery(id+"F1.imprint","IMPRINT",EDGE,{"derivedFrom":sQuery(id+"F1.wireOp",EDGE,"E5.1.2.0")}),1.0]])]});
            var Q71;
            Q71=makeQuery(id+"F1.imprint","IMPRINT",FACE,{"disambiguationData":[TD([[makeQuery(id+"F1.imprint","IMPRINT",EDGE,{"derivedFrom":sQuery(id+"F1.wireOp",EDGE,"E5.2.1.0")}),1.0]])]});
            var Q72;
            Q72=makeQuery(id+"F1.imprint","IMPRINT",FACE,{"disambiguationData":[TD([[makeQuery(id+"F1.imprint","IMPRINT",EDGE,{"derivedFrom":sQuery(id+"F1.wireOp",EDGE,"E14.MirrorC")}),-1.0]])]});
            var Q73;
            Q73=makeQuery(id+"F1.imprint","IMPRINT",FACE,{"disambiguationData":[TD([[makeQuery(id+"F1.imprint","IMPRINT",EDGE,{"derivedFrom":sQuery(id+"F1.wireOp",EDGE,"E5.2.2.0")}),1.0]])]});
            var Q74;
            {var subQ0=sQuery(id+"F1.wireOp",EDGE,"E24.MirrorC");var subQ1=makeQuery(id+"F1.imprint","INTERSECT",VERTEX,{"derivedFrom":[subQ0,sQuery(id+"F1.wireOp",EDGE,"E66.0.left")]});Q74=makeQuery(id+"F1.imprint","IMPRINT",FACE,{"disambiguationData":[TD([[makeQuery(id+"F1.imprint","IMPRINT",EDGE,{"disambiguationData":[TD([[subQ1,1.0]])],"derivedFrom":subQ0}),-1.0]])]});}
            var Q75;
            Q75=makeQuery(id+"F1.imprint","IMPRINT",FACE,{"disambiguationData":[TD([[makeQuery(id+"F1.imprint","IMPRINT",EDGE,{"derivedFrom":sQuery(id+"F1.wireOp",EDGE,"E5.2.3.0")}),1.0]])]});
            var Q76;
            Q76=makeQuery(id+"F1.imprint","IMPRINT",FACE,{"disambiguationData":[TD([[makeQuery(id+"F1.imprint","IMPRINT",EDGE,{"derivedFrom":sQuery(id+"F1.wireOp",EDGE,"E5.3.0.1")}),-1.0]])]});
            var Q77;
            Q77=makeQuery(id+"F1.imprint","IMPRINT",FACE,{"disambiguationData":[TD([[makeQuery(id+"F1.imprint","IMPRINT",EDGE,{"derivedFrom":sQuery(id+"F1.wireOp",EDGE,"E18.MirrorC")}),-1.0]])]});
            var Q78;
            Q78=makeQuery(id+"F1.imprint","IMPRINT",FACE,{"disambiguationData":[TD([[makeQuery(id+"F1.imprint","IMPRINT",EDGE,{"derivedFrom":sQuery(id+"F1.wireOp",EDGE,"E5.3.1.0")}),1.0]])]});
            var Q79;
            Q79=makeQuery(id+"F1.imprint","IMPRINT",FACE,{"disambiguationData":[TD([[makeQuery(id+"F1.imprint","IMPRINT",EDGE,{"derivedFrom":sQuery(id+"F1.wireOp",EDGE,"E5.3.2.0")}),1.0]])]});
            var Q80;
            Q80=makeQuery(id+"F1.imprint","IMPRINT",FACE,{"disambiguationData":[TD([[makeQuery(id+"F1.imprint","IMPRINT",EDGE,{"derivedFrom":sQuery(id+"F1.wireOp",EDGE,"E5.4.1.0")}),1.0]])]});
            var Q81;
            Q81=makeQuery(id+"F1.imprint","IMPRINT",FACE,{"disambiguationData":[TD([[makeQuery(id+"F1.imprint","IMPRINT",EDGE,{"derivedFrom":sQuery(id+"F1.wireOp",EDGE,"E5.3.3.0")}),1.0]])]});
            var Q82;
            Q82=makeQuery(id+"F1.imprint","IMPRINT",FACE,{"disambiguationData":[TD([[makeQuery(id+"F1.imprint","IMPRINT",EDGE,{"derivedFrom":sQuery(id+"F1.wireOp",EDGE,"E5.4.2.0")}),1.0]])]});
            var Q83;
            Q83=makeQuery(id+"F1.imprint","IMPRINT",FACE,{"disambiguationData":[TD([[makeQuery(id+"F1.imprint","IMPRINT",EDGE,{"derivedFrom":sQuery(id+"F1.wireOp",EDGE,"E5.4.3.0")}),1.0]])]});
            var Q84;
            Q84=makeQuery(id+"F1.imprint","IMPRINT",FACE,{"disambiguationData":[TD([[makeQuery(id+"F1.imprint","IMPRINT",EDGE,{"derivedFrom":sQuery(id+"F1.wireOp",EDGE,"E9.MirrorC")}),-1.0]])]});
            var Q85;
            Q85=makeQuery(id+"F1.imprint","IMPRINT",FACE,{"disambiguationData":[TD([[makeQuery(id+"F1.imprint","IMPRINT",EDGE,{"derivedFrom":sQuery(id+"F1.wireOp",EDGE,"E5.0.2.0")}),-1.0]])]});
            var Q86;
            Q86=makeQuery(id+"F1.imprint","IMPRINT",FACE,{"disambiguationData":[TD([[makeQuery(id+"F1.imprint","IMPRINT",EDGE,{"derivedFrom":sQuery(id+"F1.wireOp",EDGE,"E5.4.0.1")}),-1.0]])]});
            var Q87;
            Q87=makeQuery(id+"F1.imprint","IMPRINT",FACE,{"disambiguationData":[TD([[makeQuery(id+"F1.imprint","IMPRINT",EDGE,{"derivedFrom":sQuery(id+"F1.wireOp",EDGE,"E7.MirrorC")}),1.0]])]});
            var Q88;
            Q88=makeQuery(id+"F1.imprint","IMPRINT",FACE,{"disambiguationData":[TD([[makeQuery(id+"F1.imprint","IMPRINT",EDGE,{"derivedFrom":sQuery(id+"F1.wireOp",EDGE,"E16.MirrorC")}),-1.0]])]});
            var Q89;
            Q89=makeQuery(id+"F1.imprint","IMPRINT",FACE,{"disambiguationData":[TD([[makeQuery(id+"F1.imprint","IMPRINT",EDGE,{"derivedFrom":sQuery(id+"F1.wireOp",EDGE,"E5.1.0.1")}),-1.0]])]});
            var Q90;
            {var subQ0=sQuery(id+"F1.wireOp",EDGE,"E5.4.3.1");var subQ1=makeQuery(id+"F1.imprint","INTERSECT",VERTEX,{"derivedFrom":[subQ0,sQuery(id+"F1.wireOp",EDGE,"E62.0.left")]});Q90=makeQuery(id+"F1.imprint","IMPRINT",FACE,{"disambiguationData":[TD([[makeQuery(id+"F1.imprint","IMPRINT",EDGE,{"disambiguationData":[TD([[subQ1,-1.0]])],"derivedFrom":subQ0}),1.0]])]});}
            var Q91;
            Q91=makeQuery(id+"F1.imprint","IMPRINT",FACE,{"disambiguationData":[TD([[makeQuery(id+"F1.imprint","IMPRINT",EDGE,{"derivedFrom":sQuery(id+"F1.wireOp",EDGE,"E27.MirrorC")}),-1.0]])]});
            var Q92;
            {var subQ0=sQuery(id+"F1.wireOp",EDGE,"E55.MirrorC");var subQ1=makeQuery(id+"F1.imprint","INTERSECT",VERTEX,{"derivedFrom":[subQ0,sQuery(id+"F1.wireOp",EDGE,"E67.0.left")]});Q92=makeQuery(id+"F1.imprint","IMPRINT",FACE,{"disambiguationData":[TD([[makeQuery(id+"F1.imprint","IMPRINT",EDGE,{"disambiguationData":[TD([[subQ1,-1.0]])],"derivedFrom":subQ0}),-1.0]])]});}
            var Q93;
            Q93=makeQuery(id+"F1.imprint","IMPRINT",FACE,{"disambiguationData":[TD([[makeQuery(id+"F1.imprint","IMPRINT",EDGE,{"derivedFrom":sQuery(id+"F1.wireOp",EDGE,"E5.2.0.1")}),-1.0]])]});
            var Q94;
            Q94=makeQuery(id+"F1.imprint","IMPRINT",FACE,{"disambiguationData":[TD([[makeQuery(id+"F1.imprint","IMPRINT",EDGE,{"derivedFrom":sQuery(id+"F1.wireOp",EDGE,"E5.0.3.0")}),-1.0]])]});
            var Q95;
            Q95=makeQuery(id+"F1.imprint","IMPRINT",FACE,{"disambiguationData":[TD([[makeQuery(id+"F1.imprint","IMPRINT",EDGE,{"derivedFrom":sQuery(id+"F1.wireOp",EDGE,"E5.0.1.0")}),-1.0]])]});
            var Q96;
            Q96=makeQuery(id+"F1.imprint","IMPRINT",FACE,{"disambiguationData":[TD([[makeQuery(id+"F1.imprint","IMPRINT",EDGE,{"derivedFrom":sQuery(id+"F1.wireOp",EDGE,"E6.MirrorC")}),1.0]])]});
            var Q97;
            Q97=makeQuery(id+"F1.imprint","IMPRINT",FACE,{"disambiguationData":[TD([[makeQuery(id+"F1.imprint","IMPRINT",EDGE,{"derivedFrom":sQuery(id+"F1.wireOp",EDGE,"E4")}),-1.0]])]});
            var Q98;
            Q98=makeQuery(id+"F1.imprint","IMPRINT",FACE,{"disambiguationData":[TD([[makeQuery(id+"F1.imprint","IMPRINT",EDGE,{"derivedFrom":sQuery(id+"F1.wireOp",EDGE,"E3")}),-1.0]])]});
            extrude(context, id + "F2", {"entities" : qUnion([Q0, Q1, Q2, Q3, Q4, Q5, Q6, Q7, Q8, Q9, Q10, Q11, Q12, Q13, Q14, Q15, Q16, Q17, Q18, Q19, Q20, Q21, Q22, Q23, Q24, Q25, Q26, Q27, Q28, Q29, Q30, Q31, Q32, Q33, Q34, Q35, Q36, Q37, Q38, Q39, Q40, Q41, Q42, Q43, Q44, Q45, Q46, Q47, Q48, Q49, Q50, Q51, Q52, Q53, Q54, Q55, Q56, Q57, Q58, Q59, Q60, Q61, Q62, Q63, Q64, Q65, Q66, Q67, Q68, Q69, Q70, Q71, Q72, Q73, Q74, Q75, Q76, Q77, Q78, Q79, Q80, Q81, Q82, Q83, Q84, Q85, Q86, Q87, Q88, Q89, Q90, Q91, Q92, Q93, Q94, Q95, Q96, Q97, Q98]), "depth" : 18 * mm, "offsetDistance" : 25 * mm});
        }
    });
